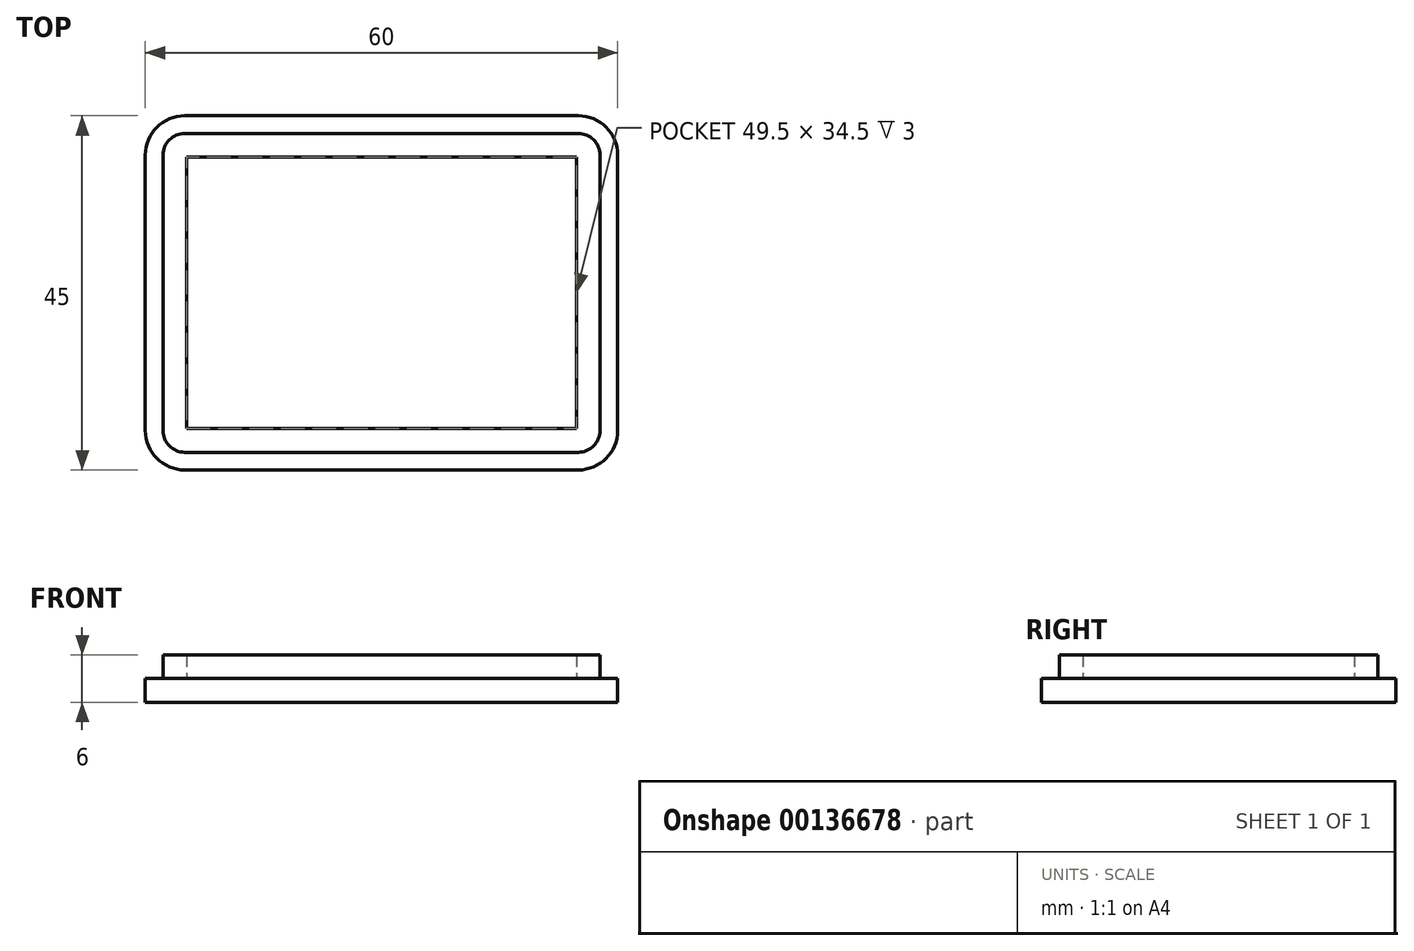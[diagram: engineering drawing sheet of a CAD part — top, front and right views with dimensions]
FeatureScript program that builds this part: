
annotation { "Feature Type Name" : "Feature", "Feature Type Description" : "" }
export const myFeature = defineFeature(function(context is Context, id is Id, definition is map)
    precondition{}
    {
        {
            var Q0;
            Q0=qCreatedBy(makeId("Top.planeOp"),FACE);
            var sketch = newSketch(context, id + "F0", { "sketchPlane" : qUnion([Q0])});
            skPoint(sketch, "E0.visualSharp", {"position": v(-28, -20.5) * mm});
            skPoint(sketch, "E1.visualSharp", {"position": v(-28, 20.5) * mm});
            skPoint(sketch, "E2.visualSharp", {"position": v(28, 20.5) * mm});
            skPoint(sketch, "E3.visualSharp", {"position": v(28, -20.5) * mm});
            skLineSegment(sketch, "E4.2", {"start": v(27.75, 17.5) * mm, "end": v(27.75, -17.5) * mm});
            skLineSegment(sketch, "E4.3", {"start": v(-25, 20.25) * mm, "end": v(25, 20.25) * mm});
            skLineSegment(sketch, "E5.trimOffspring", {"start": v(-27.75, -17.5) * mm, "end": v(-27.75, 17.5) * mm});
            skLineSegment(sketch, "E6.trimOffspring", {"start": v(25, -20.25) * mm, "end": v(-25, -20.25) * mm});
            skArc(sketch, "E7", {"start": v(-25, 20.25) * mm, "mid": v(-26.94, 19.44) * mm, "end": v(-27.75, 17.5) * mm});
            skPoint(sketch, "E7.third.point", {"position": v(-26.95, 19.44) * mm});
            skArc(sketch, "E8", {"start": v(27.75, 17.5) * mm, "mid": v(26.94, 19.44) * mm, "end": v(25, 20.25) * mm});
            skPoint(sketch, "E8.third.point", {"position": v(26.78, 19.6) * mm});
            skArc(sketch, "E9", {"start": v(25, -20.25) * mm, "mid": v(26.94, -19.44) * mm, "end": v(27.75, -17.5) * mm});
            skPoint(sketch, "E9.third.point", {"position": v(26.78, -19.6) * mm});
            skArc(sketch, "E10", {"start": v(-27.75, -17.5) * mm, "mid": v(-26.94, -19.44) * mm, "end": v(-25, -20.25) * mm});
            skPoint(sketch, "E10.third.point", {"position": v(-27.22, -19.12) * mm});
            skSolve(sketch);
        }
        {
            var Q0;
            Q0=qSketchRegion(id+"F0",true);
            extrude(context, id + "F1", {"entities" : qUnion([Q0]), "depth" : 3 * mm});
        }
        {
            var Q0;
            Q0=qCreatedBy(makeId("Top.planeOp"),FACE);
            var sketch = newSketch(context, id + "F2", { "sketchPlane" : qUnion([Q0])});
            skLineSegment(sketch, "E11", {"start": v(10, 27.5) * mm, "end": v(10, -22.5) * mm, "construction": true});
            skLineSegment(sketch, "E12", {"start": v(10, -22.5) * mm, "end": v(-25, -22.5) * mm});
            skLineSegment(sketch, "E13", {"start": v(-30, -17.5) * mm, "end": v(-30, 17.5) * mm});
            skLineSegment(sketch, "E14", {"start": v(10, -22.5) * mm, "end": v(25, -22.5) * mm});
            skLineSegment(sketch, "E15", {"start": v(30, -17.5) * mm, "end": v(30, 17.5) * mm});
            skLineSegment(sketch, "E16", {"start": v(-25, 22.5) * mm, "end": v(25, 22.5) * mm});
            skPoint(sketch, "E17.visualSharp", {"position": v(-30, -22.5) * mm});
            skArc(sketch, "E17.filletArc", {"start": v(-30, -17.5) * mm, "mid": v(-28.54, -21.04) * mm, "end": v(-25, -22.5) * mm});
            skPoint(sketch, "E18.visualSharp", {"position": v(30, -22.5) * mm});
            skArc(sketch, "E18.filletArc", {"start": v(25, -22.5) * mm, "mid": v(28.54, -21.04) * mm, "end": v(30, -17.5) * mm});
            skPoint(sketch, "E19.visualSharp", {"position": v(-30, 22.5) * mm});
            skArc(sketch, "E19.filletArc", {"start": v(-25, 22.5) * mm, "mid": v(-28.54, 21.04) * mm, "end": v(-30, 17.5) * mm});
            skPoint(sketch, "E20.visualSharp", {"position": v(30, 22.5) * mm});
            skArc(sketch, "E20.filletArc", {"start": v(30, 17.5) * mm, "mid": v(28.54, 21.04) * mm, "end": v(25, 22.5) * mm});
            skSolve(sketch);
        }
        {
            var Q0;
            Q0=qSketchRegion(id+"F2",true);
            extrude(context, id + "F3", {"entities" : qUnion([Q0]), "operationType" : NewBodyOperationType.ADD, "oppositeDirection" : true, "depth" : 3 * mm});
        }
        {
            var Q0;
            Q0=makeQuery(id+"F1.opExtrude","CAP_FACE",FACE,{"disambiguationData":[OSD([sQuery(id+"F0.wireOp",EDGE,"E4.2"),sQuery(id+"F0.wireOp",EDGE,"E4.3"),sQuery(id+"F0.wireOp",EDGE,"E5.trimOffspring"),sQuery(id+"F0.wireOp",EDGE,"E6.trimOffspring"),sQuery(id+"F0.wireOp",EDGE,"E7"),sQuery(id+"F0.wireOp",EDGE,"E8"),sQuery(id+"F0.wireOp",EDGE,"E9"),sQuery(id+"F0.wireOp",EDGE,"E10")])],"isStart":false});
            shell(context, id + "F4", {"entities" : qUnion([Q0]), "thickness" : 3 * mm});
        }
    });
